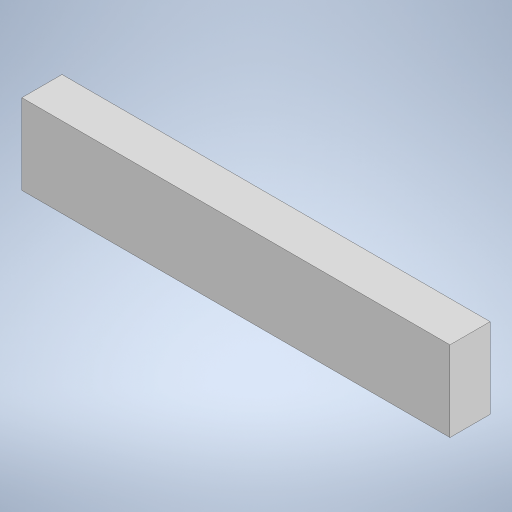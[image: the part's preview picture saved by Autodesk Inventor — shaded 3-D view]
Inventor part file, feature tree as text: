
AUTODESK INVENTOR PART (.ipt)
format: ipt  version: 2023 (Build 270158000, 158)  size: 203,264 bytes
history: native  units: mm
features: extrude x1, sketch x1
ambient origin geometry x8: Origin, YZ Plane, XZ Plane, XY Plane, X Axis, Y Axis, Z Axis, Center Point
bodies: Solid1 (feature_tree)
feature tree (2):
  extrude  "Extrusion1"  Depth=15.0mm
  sketch  "Sketch1"  dims[d0=30.0mm d1=15.0mm d2=160.0mm d3=0.0mm]
